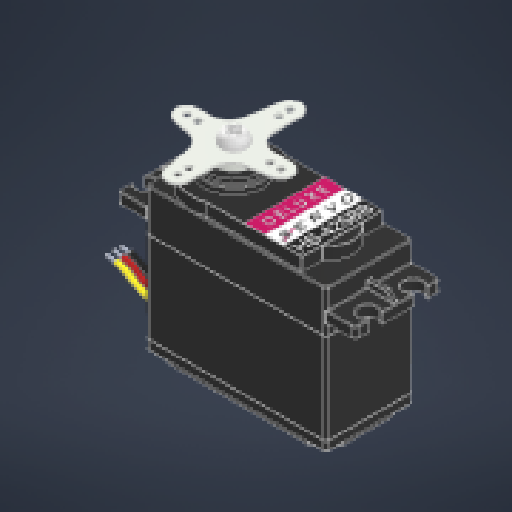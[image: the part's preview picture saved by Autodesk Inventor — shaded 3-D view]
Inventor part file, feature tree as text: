
AUTODESK INVENTOR PART (.ipt)
format: ipt  version: 2024.1 (Build 281209000, 209)  size: 1,795,072 bytes
history: native  units: in
note: dims shown in document units (in); Inventor stores cm internally (conversion verified against a paired STEP export)
features: extrude x1, sketch x1, other x1
ambient origin geometry x8: Origin, YZ Plane, XZ Plane, XY Plane, X Axis, Y Axis, Z Axis, Center Point
bodies: Solid1 (feature_tree)
feature tree (3):
  extrude  "Extrusion1"  [1 undecoded]
  sketch  "Sketch1"  dims[d0=0.0787in d1=0.0in]
  other  "Cut-Extrude11"
note: 1 required parameter value undecoded (feature->parameter linkage not recoverable at this tier; creation-order binding heuristic only, values carry confidence <= 0.55)
